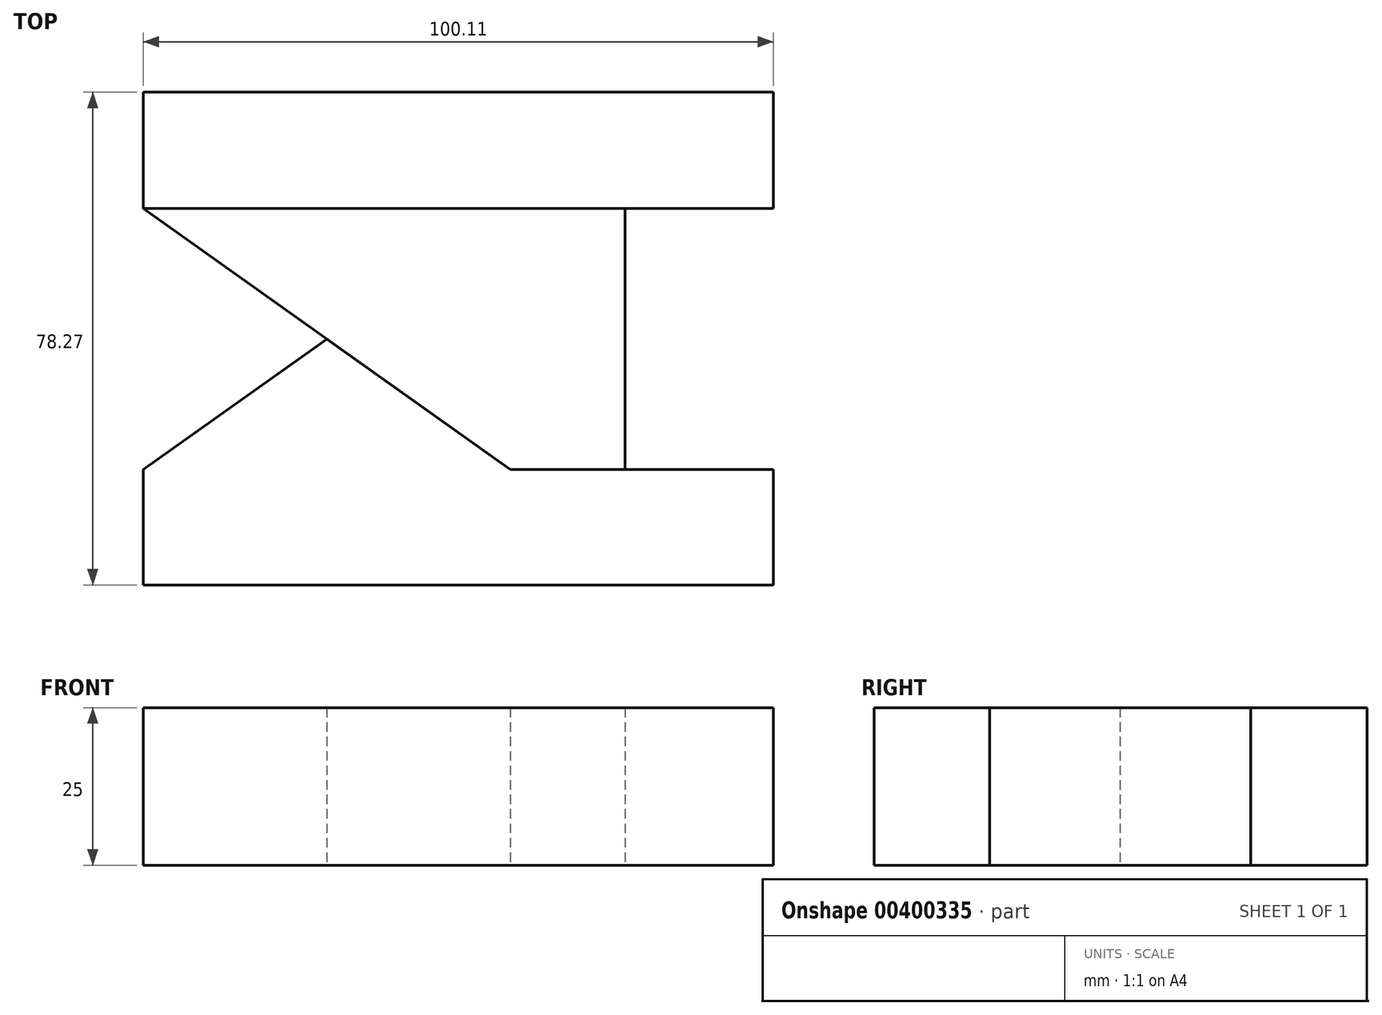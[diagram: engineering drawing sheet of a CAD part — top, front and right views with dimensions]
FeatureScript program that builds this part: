
annotation { "Feature Type Name" : "Feature", "Feature Type Description" : "" }
export const myFeature = defineFeature(function(context is Context, id is Id, definition is map)
    precondition{}
    {
        {
            var Q0;
            Q0=qCreatedBy(makeId("Top.planeOp"),FACE);
            var sketch = newSketch(context, id + "F0", { "sketchPlane" : qUnion([Q0])});
            skLineSegment(sketch, "E0.bottom", {"start": v(-20.56, 12.27) * mm, "end": v(-78.9, 12.27) * mm});
            skLineSegment(sketch, "E0.top", {"start": v(-20.56, 53.72) * mm, "end": v(-78.9, 53.72) * mm});
            skPoint(sketch, "E0.middle", {"position": v(-49.74, 33) * mm});
            skLineSegment(sketch, "E1", {"start": v(-20.56, 53.72) * mm, "end": v(-78.9, 12.27) * mm});
            skLineSegment(sketch, "E2", {"start": v(-78.9, 53.72) * mm, "end": v(-20.56, 12.27) * mm});
            skLineSegment(sketch, "E3.bottom", {"start": v(-78.9, 53.72) * mm, "end": v(21.2, 53.72) * mm});
            skLineSegment(sketch, "E3.top", {"start": v(-78.9, 72.21) * mm, "end": v(21.2, 72.21) * mm});
            skLineSegment(sketch, "E3.left", {"start": v(-78.9, 53.72) * mm, "end": v(-78.9, 72.21) * mm});
            skLineSegment(sketch, "E3.right", {"start": v(21.2, 53.72) * mm, "end": v(21.2, 72.21) * mm});
            skLineSegment(sketch, "E4.bottom", {"start": v(-78.9, 12.27) * mm, "end": v(21.2, 12.27) * mm});
            skLineSegment(sketch, "E4.top", {"start": v(-78.9, -6.06) * mm, "end": v(21.2, -6.06) * mm});
            skLineSegment(sketch, "E4.left", {"start": v(-78.9, 12.27) * mm, "end": v(-78.9, -6.06) * mm});
            skLineSegment(sketch, "E4.right", {"start": v(21.2, 12.27) * mm, "end": v(21.2, -6.06) * mm});
            skLineSegment(sketch, "E5.bottom", {"start": v(21.2, 53.72) * mm, "end": v(-2.4, 53.72) * mm});
            skLineSegment(sketch, "E5.top", {"start": v(21.2, 12.27) * mm, "end": v(-2.4, 12.27) * mm});
            skLineSegment(sketch, "E5.left", {"start": v(21.2, 53.72) * mm, "end": v(21.2, 12.27) * mm});
            skLineSegment(sketch, "E5.right", {"start": v(-2.4, 53.72) * mm, "end": v(-2.4, 12.27) * mm});
            skSolve(sketch);
        }
        {
            var Q0;
            Q0=makeQuery(id+"F0.imprint","IMPRINT",FACE,{"disambiguationData":[TD([[makeQuery(id+"F0.imprint","IMPRINT",EDGE,{"derivedFrom":sQuery(id+"F0.wireOp",EDGE,"E4.top")}),1.0]])]});
            var Q1;
            Q1=makeQuery(id+"F0.imprint","IMPRINT",FACE,{"disambiguationData":[TD([[makeQuery(id+"F0.imprint","IMPRINT",EDGE,{"derivedFrom":sQuery(id+"F0.wireOp",EDGE,"E5.bottom")}),1.0]])]});
            var Q2;
            Q2=makeQuery(id+"F0.imprint","IMPRINT",FACE,{"disambiguationData":[TD([[makeQuery(id+"F0.imprint","IMPRINT",EDGE,{"derivedFrom":sQuery(id+"F0.wireOp",EDGE,"E3.top")}),-1.0]])]});
            var Q3;
            {var subQ0=sQuery(id+"F0.wireOp",EDGE,"E4.bottom");var subQ3=sQuery(id+"F0.wireOp",EDGE,"E2");var subQ5=makeQuery(id+"F0.imprint","INTERSECT",VERTEX,{"derivedFrom":[subQ3,subQ0]});Q3=makeQuery(id+"F0.imprint","IMPRINT",FACE,{"disambiguationData":[TD([[makeQuery(id+"F0.imprint","IMPRINT",EDGE,{"disambiguationData":[TD([[subQ5,1.0]])],"derivedFrom":subQ3}),-1.0]])]});}
            extrude(context, id + "F1", {"entities" : qUnion([Q0, Q1, Q2, Q3]), "depth" : 25 * mm});
        }
        {
            var Q0;
            {var subQ0=sQuery(id+"F0.wireOp",EDGE,"E3.bottom");var subQ1=sQuery(id+"F0.wireOp",EDGE,"E1");var subQ2=makeQuery(id+"F0.imprint","INTERSECT",VERTEX,{"derivedFrom":[subQ1,subQ0]});Q0=makeQuery(id+"F0.imprint","IMPRINT",FACE,{"disambiguationData":[TD([[makeQuery(id+"F0.imprint","IMPRINT",EDGE,{"disambiguationData":[TD([[subQ2,-1.0]])],"derivedFrom":subQ1}),-1.0]])]});}
            var Q1;
            {var subQ5=sQuery(id+"F0.wireOp",EDGE,"E5.right");Q1=makeQuery(id+"F0.imprint","IMPRINT",FACE,{"disambiguationData":[TD([[makeQuery(id+"F0.imprint","IMPRINT",EDGE,{"derivedFrom":subQ5}),-1.0]])]});}
            extrude(context, id + "F2", {"entities" : qUnion([Q0, Q1]), "depth" : 25 * mm});
        }
    });
